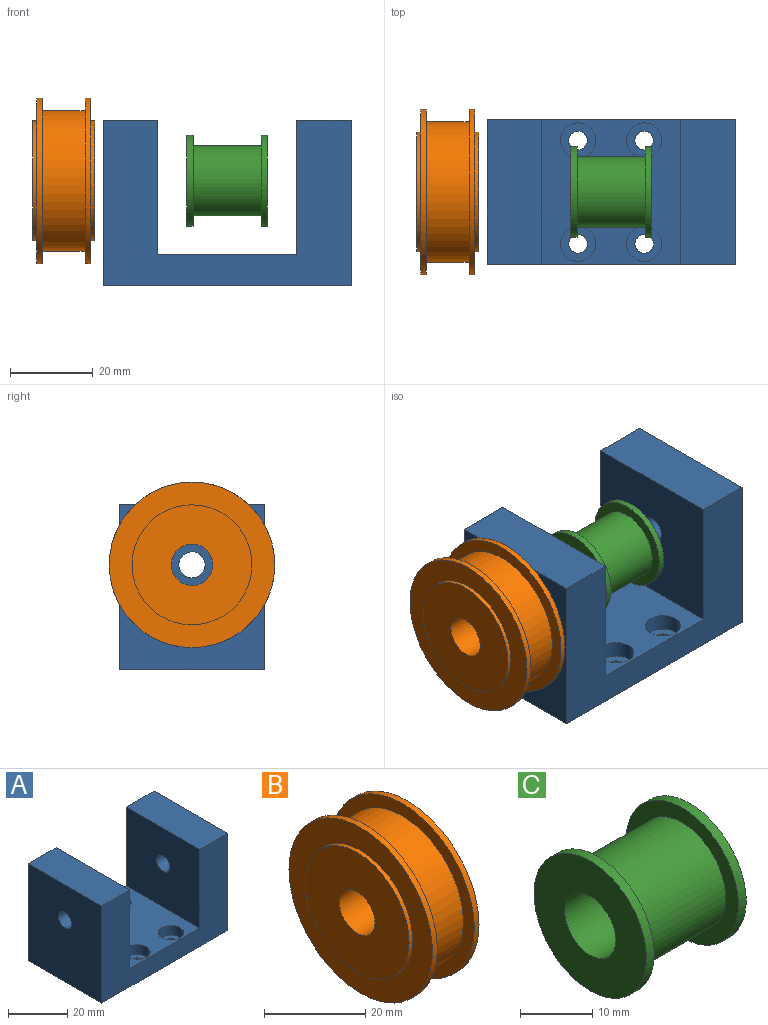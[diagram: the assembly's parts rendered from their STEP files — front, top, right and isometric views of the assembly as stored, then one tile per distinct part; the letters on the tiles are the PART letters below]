
ASSEMBLY  parts=3 mates=2
PART A: 24 faces, bbox 60x35x40 mm
  f0: plane 40x35mm, normal (1,0,0), area 1368.3mm2, adj f1,f7,f8,f9,f23
  f1: plane 35x13.25mm, normal (0,0,1), area 463.7mm2, adj f0,f2,f8,f9
  f2: plane 35x32.5mm, normal (-1,0,0), area 1105.8mm2, adj f1,f3,f8,f9,f23
  f3: plane 35x33.5mm, normal (0,0,1), area 945.5mm2, adj f2,f4,f8,f9,f10,f12,f14,f16
  f4: plane 35x32.5mm, normal (1,0,0), area 1105.8mm2, adj f3,f5,f8,f9,f22
  f5: plane 35x13.25mm, normal (0,0,1), area 463.7mm2, adj f4,f6,f8,f9
  f6: plane 40x35mm, normal (-1,0,0), area 1368.3mm2, adj f5,f7,f8,f9,f22
  f7: plane 60x35mm, normal (0,0,-1), area 2036.4mm2, adj f0,f6,f8,f9,f18,f19,f20,f21
  f8: plane 60x40mm, normal (0,-1,0), area 1311.2mm2, adj f0,f1,f2,f3,f4,f5,f6,f7
  f9: plane 60x40mm, normal (0,1,0), area 1311.2mm2, adj f0,f1,f2,f3,f4,f5,f6,f7
  f10: cylinder r=4.25mm len=8.5mm, axis (0,0,1), area 106.8mm2, adj f3,f11
  f11: plane 8.5x8.5mm, normal (0,0,1), area 40.8mm2, adj f10,f21
  f12: cylinder r=4.25mm len=8.5mm, axis (0,0,1), area 106.8mm2, adj f3,f13
  f13: plane 8.5x8.5mm, normal (0,0,1), area 40.8mm2, adj f12,f18
  f14: cylinder r=4.25mm len=8.5mm, axis (0,0,1), area 106.8mm2, adj f3,f15
  f15: plane 8.5x8.5mm, normal (0,0,1), area 40.8mm2, adj f14,f19
  f16: cylinder r=4.25mm len=8.5mm, axis (0,0,1), area 106.8mm2, adj f3,f17
  f17: plane 8.5x8.5mm, normal (0,0,1), area 40.8mm2, adj f16,f20
  f18: cylinder r=2.25mm len=4.5mm, axis (0,0,1), area 49.5mm2, adj f7,f13
  f19: cylinder r=2.25mm len=4.5mm, axis (0,0,1), area 49.5mm2, adj f7,f15
  f20: cylinder r=2.25mm len=4.5mm, axis (0,0,1), area 49.5mm2, adj f7,f17
  f21: cylinder r=2.25mm len=4.5mm, axis (0,0,1), area 49.5mm2, adj f7,f11
  f22: cylinder r=3.17mm len=13.25mm, axis (1,0,0), area 264.3mm2, adj f4,f6
  f23: cylinder r=3.17mm len=13.25mm, axis (1,0,0), area 264.3mm2, adj f0,f2
PART B: 12 faces, bbox 15x40x40 mm
  f0: cylinder r=20mm len=40mm, axis (1,0,0), area 169.6mm2, adj f3,f6
  f1: cylinder r=5mm len=15mm, axis (1,0,0), area 471.2mm2, adj f9,f11
  f2: cylinder r=20mm len=40mm, axis (1,0,0), area 169.6mm2, adj f4,f7
  f3: plane 40x40mm, normal (-1,0,0), area 596.1mm2, adj f0,f8
  f4: plane 40x40mm, normal (1,0,0), area 596.1mm2, adj f2,f10
  f5: cylinder r=17mm len=34mm, axis (1,0,0), area 1100.2mm2, adj f6,f7
  f6: plane 40x40mm, normal (1,0,0), area 348.7mm2, adj f0,f5
  f7: plane 40x40mm, normal (-1,0,0), area 348.7mm2, adj f2,f5
  f8: cylinder r=14.5mm len=29mm, axis (1,0,0), area 91.1mm2, adj f3,f9
  f9: plane 29x29mm, normal (-1,0,0), area 582mm2, adj f1,f8
  f10: cylinder r=14.5mm len=29mm, axis (-1,0,0), area 91.1mm2, adj f4,f11
  f11: plane 29x29mm, normal (1,0,0), area 582mm2, adj f1,f10
PART C: 8 faces, bbox 19.5x22x22 mm
  f0: cylinder r=11mm len=22mm, axis (-1,0,0), area 103.7mm2, adj f4,f6
  f1: cylinder r=5mm len=19.5mm, axis (-1,0,0), area 612.6mm2, adj f3,f4
  f2: cylinder r=11mm len=22mm, axis (-1,0,0), area 103.7mm2, adj f3,f7
  f3: plane 22x22mm, normal (1,0,0), area 301.6mm2, adj f1,f2
  f4: plane 22x22mm, normal (-1,0,0), area 301.6mm2, adj f0,f1
  f5: cylinder r=8.5mm len=17mm, axis (1,0,0), area 881.2mm2, adj f6,f7
  f6: plane 22x22mm, normal (1,0,0), area 153.2mm2, adj f0,f5
  f7: plane 22x22mm, normal (-1,0,0), area 153.2mm2, adj f2,f5
PLACE A at identity fixed
PLACE B t=(-1,0,0)mm
PLACE C at identity
MATE fastened C.f0 <-> A.f22  axis (1,0,0) through (0,0,25.4)mm
MATE fastened A.f22 <-> B.f0  axis (-1,0,0) through (-30,0,25.4)mm
